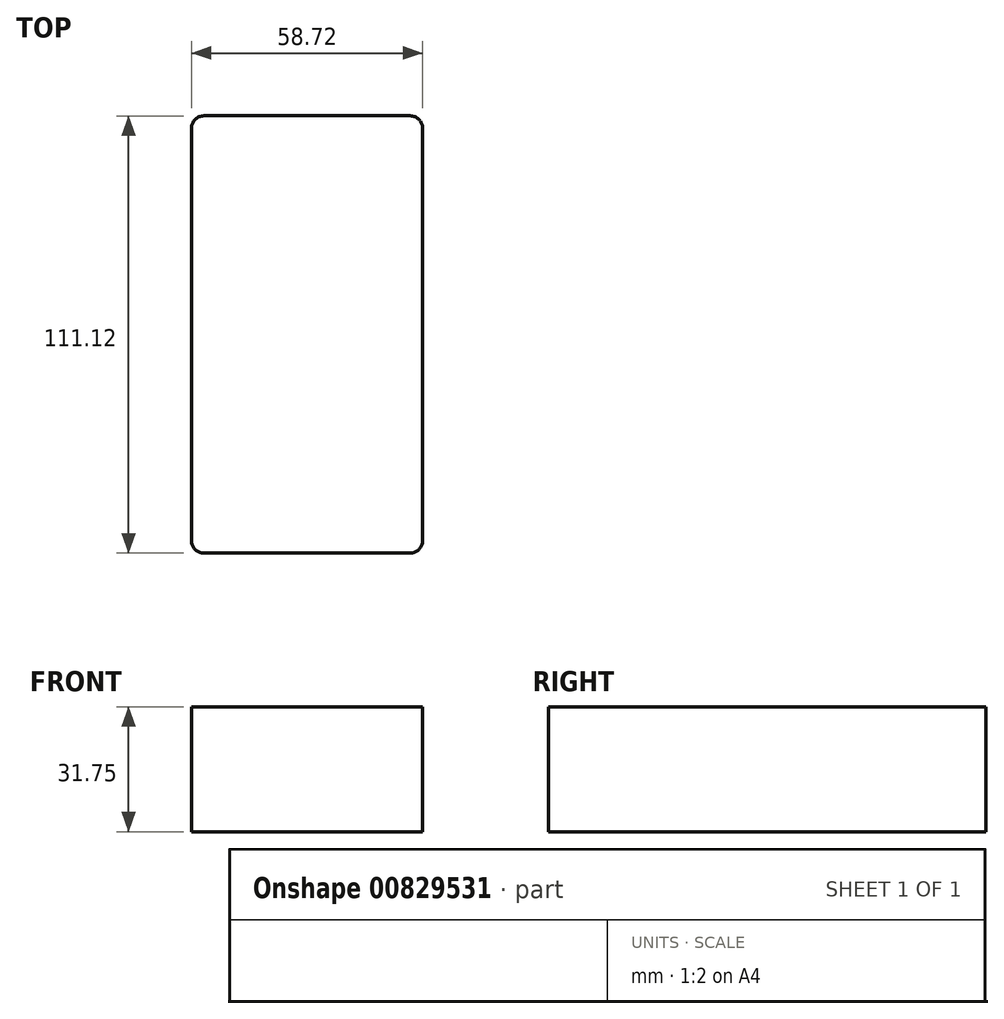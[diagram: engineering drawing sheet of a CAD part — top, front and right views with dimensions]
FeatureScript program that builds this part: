
annotation { "Feature Type Name" : "Feature", "Feature Type Description" : "" }
export const myFeature = defineFeature(function(context is Context, id is Id, definition is map)
    precondition{}
    {
        {
            var Q0;
            Q0=qCreatedBy(makeId("Top.planeOp"),FACE);
            var sketch = newSketch(context, id + "F0", { "sketchPlane" : qUnion([Q0])});
            skLineSegment(sketch, "E0.bottom", {"start": v(5.21, 0) * mm, "end": v(57.58, 0) * mm});
            skLineSegment(sketch, "E0.top", {"start": v(5.21, 111.13) * mm, "end": v(57.58, 111.13) * mm});
            skLineSegment(sketch, "E0.left", {"start": v(2.04, 3.17) * mm, "end": v(2.04, 107.95) * mm});
            skLineSegment(sketch, "E0.right", {"start": v(60.76, 3.17) * mm, "end": v(60.76, 107.95) * mm});
            skPoint(sketch, "E1.visualSharp", {"position": v(2.04, 111.13) * mm});
            skArc(sketch, "E1.filletArc", {"start": v(5.21, 111.13) * mm, "mid": v(2.96, 110.2) * mm, "end": v(2.04, 107.95) * mm});
            skPoint(sketch, "E2.visualSharp", {"position": v(60.76, 111.13) * mm});
            skArc(sketch, "E2.filletArc", {"start": v(60.76, 107.95) * mm, "mid": v(59.83, 110.2) * mm, "end": v(57.58, 111.12) * mm});
            skPoint(sketch, "E3.visualSharp", {"position": v(60.76, 0) * mm});
            skArc(sketch, "E3.filletArc", {"start": v(57.58, 0) * mm, "mid": v(59.83, 0.93) * mm, "end": v(60.76, 3.17) * mm});
            skPoint(sketch, "E4.visualSharp", {"position": v(2.04, 0) * mm});
            skArc(sketch, "E4.filletArc", {"start": v(2.04, 3.17) * mm, "mid": v(2.96, 0.93) * mm, "end": v(5.21, 0) * mm});
            skSolve(sketch);
        }
        {
            var Q0;
            Q0=makeQuery(id+"F0.imprint","IMPRINT",FACE,{"disambiguationData":[TD([[makeQuery(id+"F0.imprint","IMPRINT",EDGE,{"derivedFrom":sQuery(id+"F0.wireOp",EDGE,"E0.bottom")}),1.0]])]});
            extrude(context, id + "F1", {"entities" : qUnion([Q0]), "depth" : 31.75 * mm, "offsetDistance" : 25.4 * mm});
        }
    });
